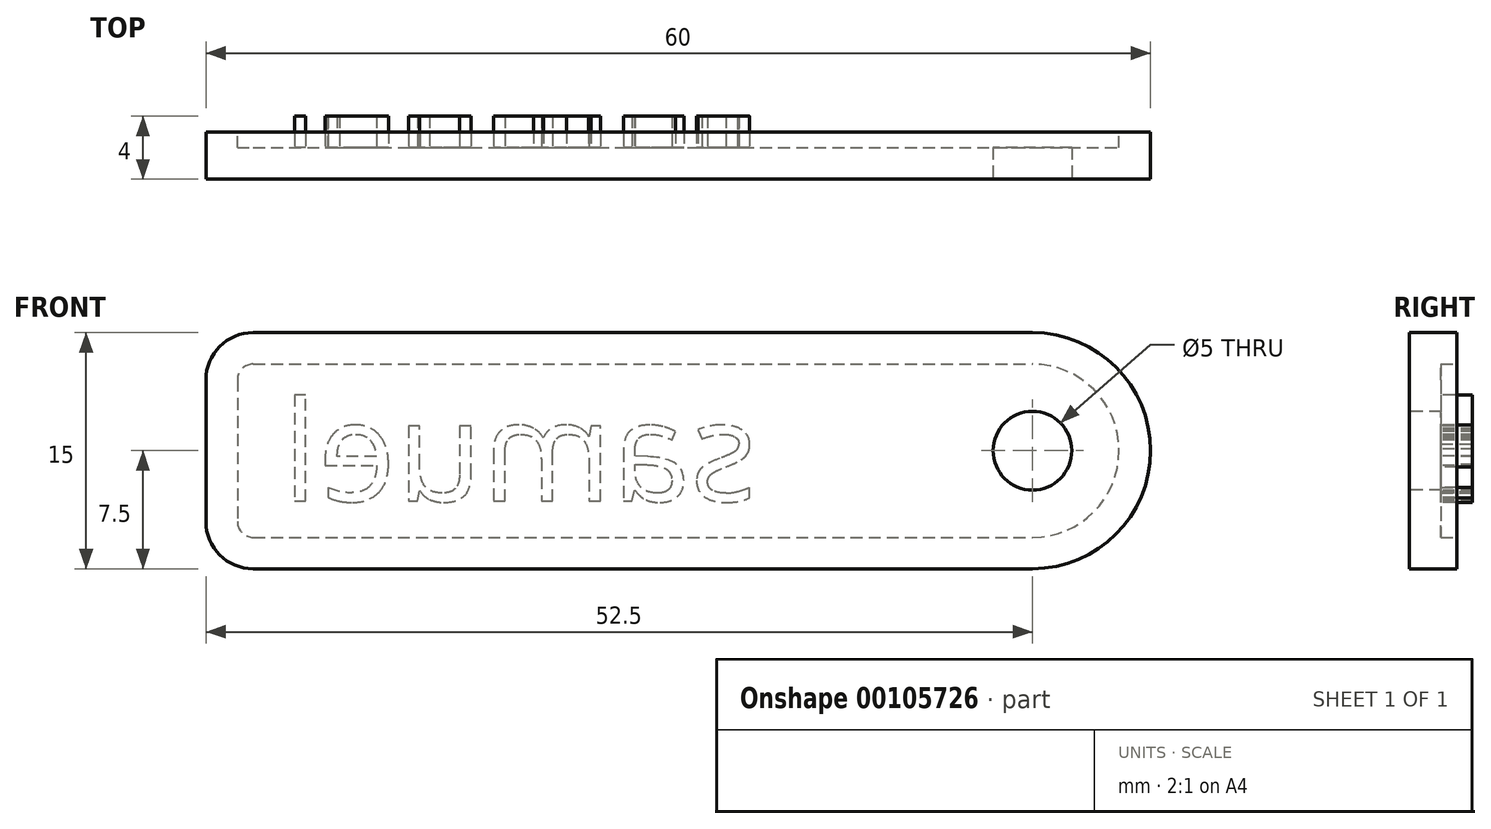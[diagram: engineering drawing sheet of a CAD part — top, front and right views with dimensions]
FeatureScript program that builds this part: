
annotation { "Feature Type Name" : "Feature", "Feature Type Description" : "" }
export const myFeature = defineFeature(function(context is Context, id is Id, definition is map)
    precondition{}
    {
        {
            var Q0;
            Q0=qCreatedBy(makeId("Front.planeOp"),FACE);
            var sketch = newSketch(context, id + "F0", { "sketchPlane" : qUnion([Q0])});
            skLineSegment(sketch, "E0.bottom", {"start": v(3, 15) * mm, "end": v(52.5, 15) * mm});
            skLineSegment(sketch, "E0.top", {"start": v(3, 0) * mm, "end": v(52.5, 0) * mm});
            skLineSegment(sketch, "E0.left", {"start": v(0, 12) * mm, "end": v(0, 3) * mm});
            skArc(sketch, "E1", {"start": v(52.5, 15) * mm, "mid": v(60, 7.5) * mm, "end": v(52.5, 0) * mm});
            skPoint(sketch, "E2.visualSharp", {"position": v(0, 15) * mm});
            skArc(sketch, "E2.filletArc", {"start": v(3, 15) * mm, "mid": v(0.88, 14.12) * mm, "end": v(0, 12) * mm});
            skPoint(sketch, "E3.visualSharp", {"position": v(0, 0) * mm});
            skArc(sketch, "E3.filletArc", {"start": v(0, 3) * mm, "mid": v(0.88, 0.88) * mm, "end": v(3, 0) * mm});
            skCircle(sketch, "E4", {"center": v(52.5, 7.5) * mm, "radius": 2.5 * mm});
            skSolve(sketch);
        }
        {
            var Q0;
            Q0=makeQuery(id+"F0.imprint","IMPRINT",FACE,{"disambiguationData":[TD([[makeQuery(id+"F0.imprint","IMPRINT",EDGE,{"derivedFrom":sQuery(id+"F0.wireOp",EDGE,"E0.bottom")}),-1.0]])]});
            extrude(context, id + "F1", {"entities" : qUnion([Q0]), "oppositeDirection" : true, "depth" : 3 * mm});
        }
        {
            var Q0;
            Q0=makeQuery(id+"F1.opExtrude","CAP_FACE",FACE,{"disambiguationData":[OSD([sQuery(id+"F0.wireOp",EDGE,"E0.bottom"),sQuery(id+"F0.wireOp",EDGE,"E0.top"),sQuery(id+"F0.wireOp",EDGE,"E0.left"),sQuery(id+"F0.wireOp",EDGE,"E1"),sQuery(id+"F0.wireOp",EDGE,"E2.filletArc"),sQuery(id+"F0.wireOp",EDGE,"E3.filletArc"),sQuery(id+"F0.wireOp",EDGE,"E4")])],"isStart":false});
            var sketch = newSketch(context, id + "F2", { "sketchPlane" : qUnion([Q0])});
            skText(sketch, "E5", { "text": "samuel", "fontName": "OpenSans-Regular.ttf"});
            skLineSegment(sketch, "E6", {"start": v(-52.5, 7.5) * mm, "end": v(0, 7.5) * mm, "construction": true});
            const initialGuessF2  = {"E5": [-0.035, 0.0043, 1, 0, 0.0064]};
            skSetInitialGuess(sketch, initialGuessF2);
            skSolve(sketch);
        }
        {
            var Q0;
            Q0 = qSketchRegion(id + "F2", true);
            extrude(context, id + "F3", {"entities" : qUnion([Q0]), "operationType" : NewBodyOperationType.ADD, "depth" : 1 * mm});
        }
        {
            var Q0;
            {var subQ0=sQuery(id+"F0.wireOp",EDGE,"E4");var subQ1=sQuery(id+"F0.wireOp",EDGE,"E0.left");var subQ2=sQuery(id+"F0.wireOp",EDGE,"E3.filletArc");var subQ3=sQuery(id+"F0.wireOp",EDGE,"E0.bottom");var subQ4=sQuery(id+"F0.wireOp",EDGE,"E1");var subQ5=sQuery(id+"F0.wireOp",EDGE,"E0.top");var subQ6=sQuery(id+"F0.wireOp",EDGE,"E2.filletArc");Q0=makeQuery(id+"F3.boolean.opBoolean","SPLIT",FACE,{"disambiguationData":[TD([makeQuery(id+"F1.opExtrude","SWEPT_FACE",FACE,{"disambiguationData":[OSD([subQ3])]})])],"derivedFrom":makeQuery(id+"F1.opExtrude","CAP_FACE",FACE,{"disambiguationData":[OSD([subQ3,subQ5,subQ1,subQ4,subQ6,subQ2,subQ0])],"isStart":false})});}
            var sketch = newSketch(context, id + "F4", { "sketchPlane" : qUnion([Q0])});
            skArc(sketch, "E7.0", {"start": v(-3, 13) * mm, "mid": v(-2.3, 12.7) * mm, "end": v(-2, 12) * mm});
            skArc(sketch, "E7.1", {"start": v(-52.5, 13) * mm, "mid": v(-58, 7.5) * mm, "end": v(-52.5, 2) * mm});
            skLineSegment(sketch, "E7.2", {"start": v(-3, 2) * mm, "end": v(-52.5, 2) * mm});
            skLineSegment(sketch, "E7.3", {"start": v(-3, 13) * mm, "end": v(-52.5, 13) * mm});
            skArc(sketch, "E7.4", {"start": v(-2, 3) * mm, "mid": v(-2.3, 2.3) * mm, "end": v(-3, 2) * mm});
            skLineSegment(sketch, "E7.5", {"start": v(-2, 12) * mm, "end": v(-2, 3) * mm});
            skLineSegment(sketch, "E8.0", {"start": v(-3, 13.5) * mm, "end": v(-52.5, 13.5) * mm});
            skLineSegment(sketch, "E8.1", {"start": v(-3, 1.5) * mm, "end": v(-52.5, 1.5) * mm});
            skArc(sketch, "E8.2", {"start": v(-1.5, 3) * mm, "mid": v(-1.94, 1.94) * mm, "end": v(-3, 1.5) * mm});
            skArc(sketch, "E8.3", {"start": v(-52.5, 13.5) * mm, "mid": v(-58.5, 7.5) * mm, "end": v(-52.5, 1.5) * mm});
            skLineSegment(sketch, "E8.4", {"start": v(-1.5, 12) * mm, "end": v(-1.5, 3) * mm});
            skArc(sketch, "E8.5", {"start": v(-3, 13.5) * mm, "mid": v(-1.94, 13.06) * mm, "end": v(-1.5, 12) * mm});
            skSolve(sketch);
        }
        {
            var Q0;
            Q0=makeQuery(id+"F4.imprint","IMPRINT",FACE,{"disambiguationData":[TD([[makeQuery(id+"F4.imprint","IMPRINT",EDGE,{"derivedFrom":sQuery(id+"F4.wireOp",EDGE,"E7.0")}),1.0]])]});
            extrude(context, id + "F5", {"entities" : qUnion([Q0]), "operationType" : NewBodyOperationType.REMOVE, "oppositeDirection" : true, "depth" : 1 * mm});
        }
    });
